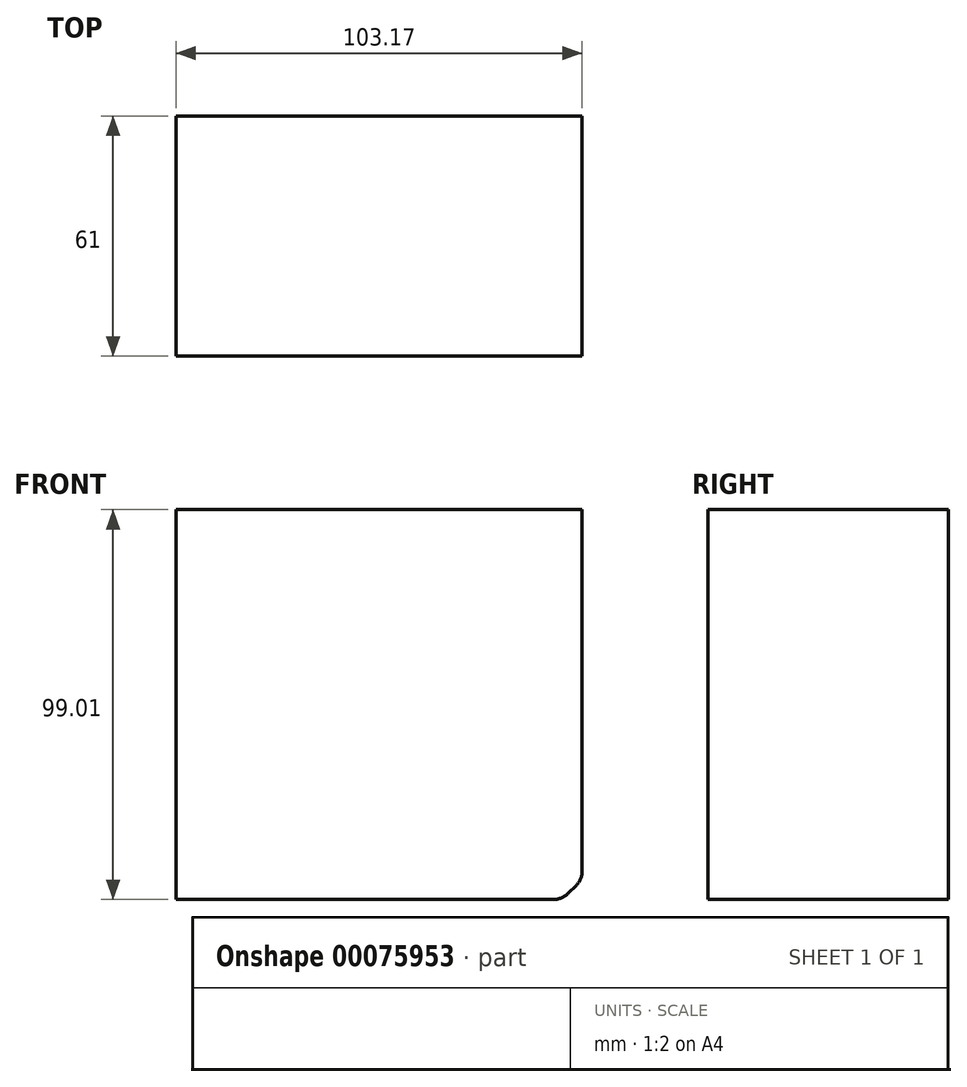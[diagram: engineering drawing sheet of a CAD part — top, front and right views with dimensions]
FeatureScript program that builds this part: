
annotation { "Feature Type Name" : "Feature", "Feature Type Description" : "" }
export const myFeature = defineFeature(function(context is Context, id is Id, definition is map)
    precondition{}
    {
        {
            var Q0;
            Q0=qCreatedBy(makeId("Front.planeOp"),FACE);
            var sketch = newSketch(context, id + "F0", { "sketchPlane" : qUnion([Q0])});
            skLineSegment(sketch, "E0.bottom", {"start": v(-51.7, 51.8) * mm, "end": v(51.47, 51.8) * mm});
            skLineSegment(sketch, "E0.top", {"start": v(-51.7, -47.2) * mm, "end": v(51.47, -47.2) * mm});
            skLineSegment(sketch, "E0.left", {"start": v(-51.7, 51.8) * mm, "end": v(-51.7, -47.2) * mm});
            skLineSegment(sketch, "E0.right", {"start": v(51.47, 51.8) * mm, "end": v(51.47, -47.2) * mm});
            skSolve(sketch);
        }
        {
            var Q0;
            Q0=makeQuery(id+"F0.imprint","IMPRINT",FACE,{"disambiguationData":[TD([[makeQuery(id+"F0.imprint","IMPRINT",EDGE,{"derivedFrom":sQuery(id+"F0.wireOp",EDGE,"E0.bottom")}),-1.0]])]});
            extrude(context, id + "F1", {"entities" : qUnion([Q0]), "depth" : 61 * mm});
        }
        {
            var Q0;
            Q0=makeQuery(id+"F1.opExtrude","SWEPT_EDGE",EDGE,{"disambiguationData":[OSD([sQuery(id+"F0.wireOp",EDGE,"E0.top"),sQuery(id+"F0.wireOp",EDGE,"E0.right")])]});
            chamfer(context, id + "F2", {"entities" : qUnion([Q0]), "width" : 5.08 * mm, "tangentPropagation" : true});
        }
        {
            var Q0;
            {var subQ0=sQuery(id+"F0.wireOp",EDGE,"E0.right");Q0=makeQuery(id+"F2.opChamfer","BLEND_EDGE",EDGE,{"blendedFrom":[makeQuery(id+"F1.opExtrude","SWEPT_EDGE",EDGE,{"disambiguationData":[OSD([sQuery(id+"F0.wireOp",EDGE,"E0.top"),subQ0])]}),makeQuery(id+"F1.opExtrude","SWEPT_FACE",FACE,{"disambiguationData":[OSD([subQ0])]})],"blendedInto":[makeQuery(id+"F1.opExtrude","SWEPT_FACE",FACE,{"disambiguationData":[OSD([subQ0])]})]});}
            var Q1;
            {var subQ0=sQuery(id+"F0.wireOp",EDGE,"E0.top");Q1=makeQuery(id+"F2.opChamfer","BLEND_EDGE",EDGE,{"blendedFrom":[makeQuery(id+"F1.opExtrude","SWEPT_EDGE",EDGE,{"disambiguationData":[OSD([subQ0,sQuery(id+"F0.wireOp",EDGE,"E0.right")])]}),makeQuery(id+"F1.opExtrude","SWEPT_FACE",FACE,{"disambiguationData":[OSD([subQ0])]})],"blendedInto":[makeQuery(id+"F1.opExtrude","SWEPT_FACE",FACE,{"disambiguationData":[OSD([subQ0])]})]});}
            fillet(context, id + "F3", {"entities" : qUnion([Q0, Q1]), "radius" : 5.08 * mm, "tangentPropagation" : true, "allowEdgeOverflow" : false});
        }
    });
